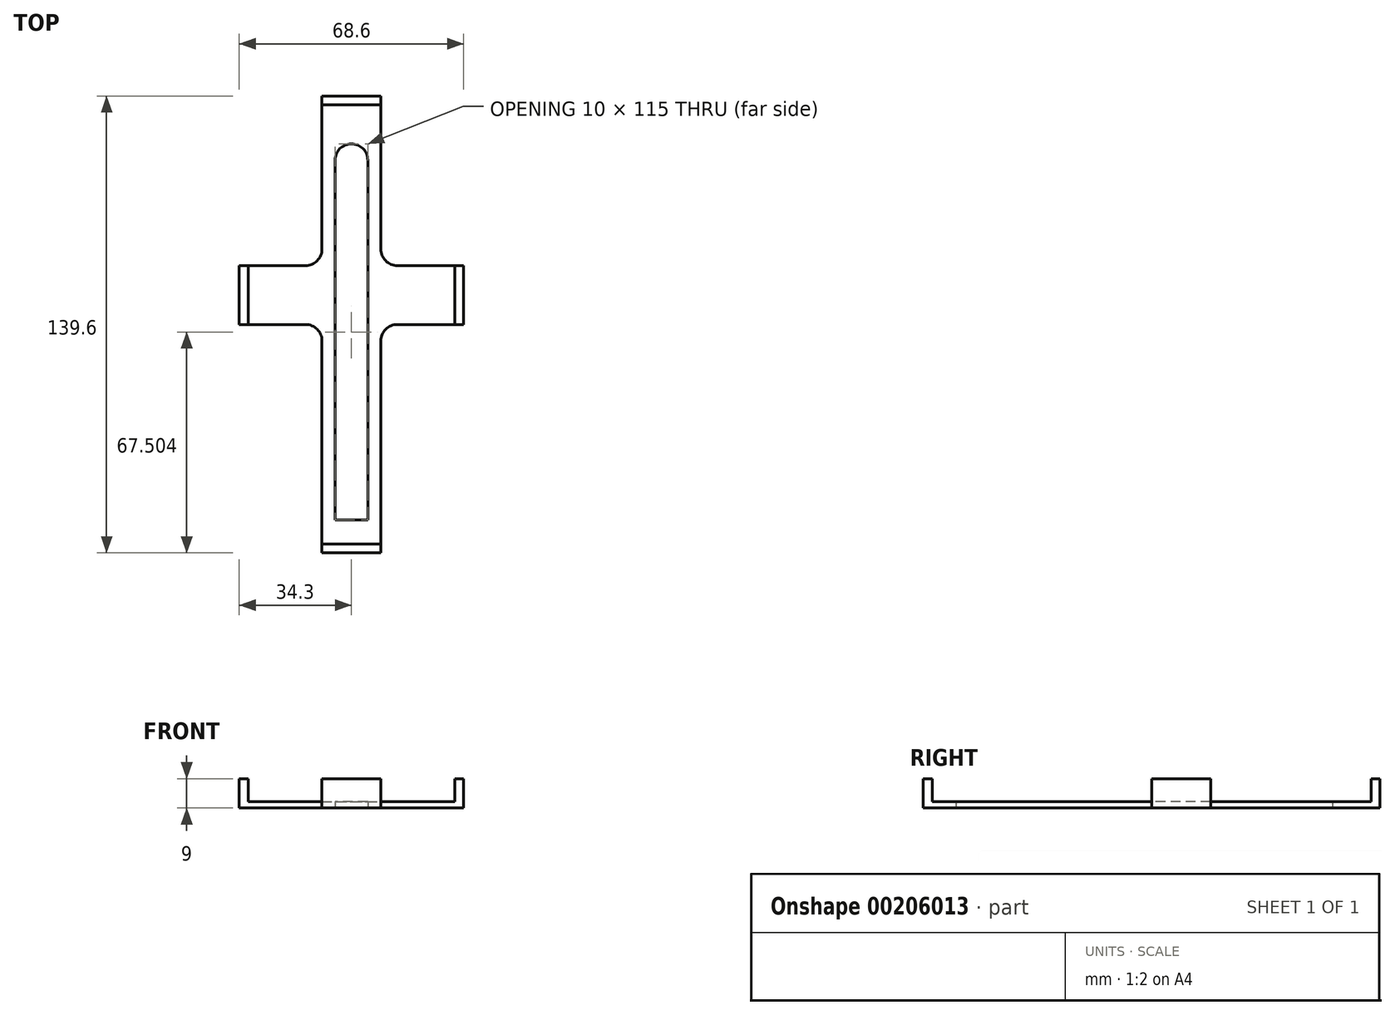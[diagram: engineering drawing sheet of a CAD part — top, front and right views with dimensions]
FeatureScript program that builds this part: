
annotation { "Feature Type Name" : "Feature", "Feature Type Description" : "" }
export const myFeature = defineFeature(function(context is Context, id is Id, definition is map)
    precondition{}
    {
        {
            var Q0;
            Q0=qCreatedBy(makeId("Top.planeOp"),FACE);
            var sketch = newSketch(context, id + "F0", { "sketchPlane" : qUnion([Q0])});
            skLineSegment(sketch, "E0.bottom", {"start": v(-9, 135.37) * mm, "end": v(9, 135.37) * mm});
            skLineSegment(sketch, "E0.top", {"start": v(-9, -4.23) * mm, "end": v(9, -4.23) * mm});
            skLineSegment(sketch, "E0.left", {"start": v(-9, 135.37) * mm, "end": v(-9, -4.23) * mm});
            skLineSegment(sketch, "E0.right", {"start": v(9, 135.37) * mm, "end": v(9, -4.23) * mm});
            skLineSegment(sketch, "E1.bottom", {"start": v(-5, 120.77) * mm, "end": v(5, 120.77) * mm});
            skLineSegment(sketch, "E1.top", {"start": v(-5, 5.77) * mm, "end": v(5, 5.77) * mm});
            skLineSegment(sketch, "E1.left", {"start": v(-5, 120.77) * mm, "end": v(-5, 5.77) * mm});
            skLineSegment(sketch, "E1.right", {"start": v(5, 120.77) * mm, "end": v(5, 5.77) * mm});
            skPoint(sketch, "E2.oppositeSnap0", {"position": v(9, 65.57) * mm});
            skLineSegment(sketch, "E2.bottom", {"start": v(-9, 83.57) * mm, "end": v(-34.3, 83.57) * mm});
            skLineSegment(sketch, "E2.top", {"start": v(-9, 65.57) * mm, "end": v(-34.3, 65.57) * mm});
            skLineSegment(sketch, "E2.left", {"start": v(-9, 83.57) * mm, "end": v(-9, 65.57) * mm});
            skLineSegment(sketch, "E2.right", {"start": v(-34.3, 83.57) * mm, "end": v(-34.3, 65.57) * mm});
            skPoint(sketch, "E3.firstSnap0", {"position": v(-21.65, 83.57) * mm});
            skPoint(sketch, "E3.oppositeSnap0", {"position": v(-21.65, 65.57) * mm});
            skLineSegment(sketch, "E3.bottom", {"start": v(9, 83.57) * mm, "end": v(34.3, 83.57) * mm});
            skLineSegment(sketch, "E3.top", {"start": v(9, 65.57) * mm, "end": v(34.3, 65.57) * mm});
            skLineSegment(sketch, "E3.left", {"start": v(9, 83.57) * mm, "end": v(9, 65.57) * mm});
            skLineSegment(sketch, "E3.right", {"start": v(34.3, 83.57) * mm, "end": v(34.3, 65.57) * mm});
            skSolve(sketch);
        }
        {
            var Q0;
            Q0=qSketchRegion(id+"F0",true);
            extrude(context, id + "F1", {"entities" : qUnion([Q0]), "depth" : 2 * mm});
        }
        {
            var Q0;
            Q0=makeQuery(id+"F1.opExtrude","CAP_FACE",FACE,{"disambiguationData":[OSD([sQuery(id+"F0.wireOp",EDGE,"E0.bottom"),sQuery(id+"F0.wireOp",EDGE,"E0.top"),sQuery(id+"F0.wireOp",EDGE,"E0.left"),sQuery(id+"F0.wireOp",EDGE,"E0.right"),sQuery(id+"F0.wireOp",EDGE,"E1.bottom"),sQuery(id+"F0.wireOp",EDGE,"E1.top"),sQuery(id+"F0.wireOp",EDGE,"E1.left"),sQuery(id+"F0.wireOp",EDGE,"E1.right"),sQuery(id+"F0.wireOp",EDGE,"E2.bottom"),sQuery(id+"F0.wireOp",EDGE,"E2.top"),sQuery(id+"F0.wireOp",EDGE,"E2.right"),sQuery(id+"F0.wireOp",EDGE,"E3.bottom"),sQuery(id+"F0.wireOp",EDGE,"E3.top"),sQuery(id+"F0.wireOp",EDGE,"E3.right")])],"isStart":false});
            var sketch = newSketch(context, id + "F2", { "sketchPlane" : qUnion([Q0])});
            skSolve(sketch);
        }
        {
            var Q0;
            {var subQ4=sQuery(id+"F0.wireOp",EDGE,"E0.bottom");Q0=makeQuery(id+"F2.imprint","IMPRINT",FACE,{"disambiguationData":[TD([[makeQuery(id+"F2.imprint","IMPRINT",EDGE,{"derivedFrom":makeQuery(id+"F1.opExtrude","CAP_EDGE",EDGE,{"disambiguationData":[OSD([subQ4])],"isStart":false})}),-1.0]])]});}
            var sketch = newSketch(context, id + "F3", { "sketchPlane" : qUnion([Q0])});
            skLineSegment(sketch, "E4.bottom", {"start": v(-34.3, 83.57) * mm, "end": v(-31.6, 83.57) * mm});
            skLineSegment(sketch, "E4.top", {"start": v(-34.3, 65.57) * mm, "end": v(-31.6, 65.57) * mm});
            skLineSegment(sketch, "E4.left", {"start": v(-34.3, 83.57) * mm, "end": v(-34.3, 65.57) * mm});
            skLineSegment(sketch, "E4.right", {"start": v(-31.6, 83.57) * mm, "end": v(-31.6, 65.57) * mm});
            skLineSegment(sketch, "E5.bottom", {"start": v(34.3, 83.57) * mm, "end": v(31.6, 83.57) * mm});
            skLineSegment(sketch, "E5.top", {"start": v(34.3, 65.57) * mm, "end": v(31.6, 65.57) * mm});
            skLineSegment(sketch, "E5.left", {"start": v(34.3, 83.57) * mm, "end": v(34.3, 65.57) * mm});
            skLineSegment(sketch, "E5.right", {"start": v(31.6, 83.57) * mm, "end": v(31.6, 65.57) * mm});
            skLineSegment(sketch, "E6.bottom", {"start": v(-9, 135.37) * mm, "end": v(9, 135.37) * mm});
            skLineSegment(sketch, "E6.top", {"start": v(-9, 132.67) * mm, "end": v(9, 132.67) * mm});
            skLineSegment(sketch, "E6.left", {"start": v(-9, 135.37) * mm, "end": v(-9, 132.67) * mm});
            skLineSegment(sketch, "E6.right", {"start": v(9, 135.37) * mm, "end": v(9, 132.67) * mm});
            skLineSegment(sketch, "E7.bottom", {"start": v(-9, -4.23) * mm, "end": v(9, -4.23) * mm});
            skLineSegment(sketch, "E7.top", {"start": v(-9, -1.53) * mm, "end": v(9, -1.53) * mm});
            skLineSegment(sketch, "E7.left", {"start": v(-9, -4.23) * mm, "end": v(-9, -1.53) * mm});
            skLineSegment(sketch, "E7.right", {"start": v(9, -4.23) * mm, "end": v(9, -1.53) * mm});
            skSolve(sketch);
        }
        {
            var Q0;
            Q0=qSketchRegion(id+"F3",true);
            extrude(context, id + "F4", {"entities" : qUnion([Q0]), "operationType" : NewBodyOperationType.ADD, "depth" : 7 * mm});
        }
        {
            var Q0;
            Q0=makeQuery(id+"F1.opExtrude","SWEPT_EDGE",EDGE,{"disambiguationData":[OSD([sQuery(id+"F0.wireOp",EDGE,"E0.left"),sQuery(id+"F0.wireOp",EDGE,"E2.top"),sQuery(id+"F0.wireOp",EDGE,"E2.left")])]});
            var Q1;
            Q1=makeQuery(id+"F1.opExtrude","SWEPT_EDGE",EDGE,{"disambiguationData":[OSD([sQuery(id+"F0.wireOp",EDGE,"E0.right"),sQuery(id+"F0.wireOp",EDGE,"E3.top"),sQuery(id+"F0.wireOp",EDGE,"E3.left")])]});
            var Q2;
            Q2=makeQuery(id+"F1.opExtrude","SWEPT_EDGE",EDGE,{"disambiguationData":[OSD([sQuery(id+"F0.wireOp",EDGE,"E0.right"),sQuery(id+"F0.wireOp",EDGE,"E3.bottom"),sQuery(id+"F0.wireOp",EDGE,"E3.left")])]});
            var Q3;
            Q3=makeQuery(id+"F1.opExtrude","SWEPT_EDGE",EDGE,{"disambiguationData":[OSD([sQuery(id+"F0.wireOp",EDGE,"E0.left"),sQuery(id+"F0.wireOp",EDGE,"E2.bottom"),sQuery(id+"F0.wireOp",EDGE,"E2.left")])]});
            var Q4;
            Q4=makeQuery(id+"F1.opExtrude","SWEPT_EDGE",EDGE,{"disambiguationData":[OSD([sQuery(id+"F0.wireOp",EDGE,"E1.bottom"),sQuery(id+"F0.wireOp",EDGE,"E1.left")])]});
            var Q5;
            Q5=makeQuery(id+"F1.opExtrude","SWEPT_EDGE",EDGE,{"disambiguationData":[OSD([sQuery(id+"F0.wireOp",EDGE,"E1.bottom"),sQuery(id+"F0.wireOp",EDGE,"E1.right")])]});
            fillet(context, id + "F5", {"entities" : qUnion([Q0, Q1, Q2, Q3, Q4, Q5]), "radius" : 5 * mm, "tangentPropagation" : true, "allowEdgeOverflow" : false});
        }
    });
